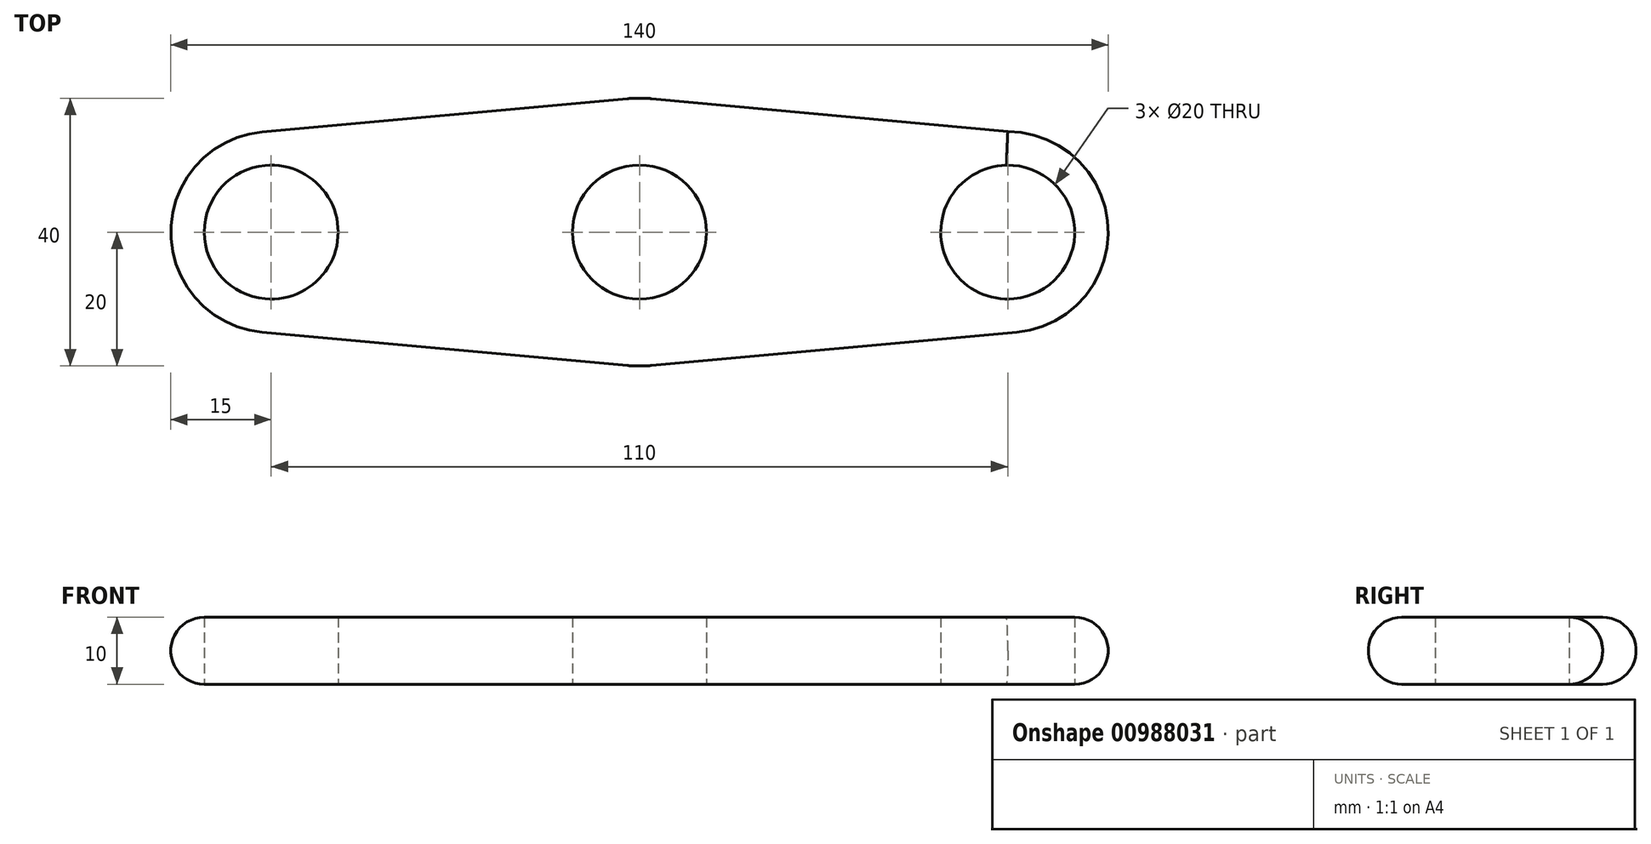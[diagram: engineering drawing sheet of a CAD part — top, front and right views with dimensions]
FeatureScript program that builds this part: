
annotation { "Feature Type Name" : "Feature", "Feature Type Description" : "" }
export const myFeature = defineFeature(function(context is Context, id is Id, definition is map)
    precondition{}
    {
        {
            var Q0;
            Q0=qCreatedBy(makeId("Top.planeOp"),FACE);
            var sketch = newSketch(context, id + "F0", { "sketchPlane" : qUnion([Q0])});
            skCircle(sketch, "E0", {"center": v(0, 0) * mm, "radius": 20 * mm});
            skCircle(sketch, "E1", {"center": v(55, 0) * mm, "radius": 15 * mm});
            skCircle(sketch, "E2", {"center": v(-55, 0) * mm, "radius": 15 * mm});
            skLineSegment(sketch, "E3", {"start": v(1.84, 19.92) * mm, "end": v(55, 15) * mm});
            skLineSegment(sketch, "E4", {"start": v(1.82, -19.92) * mm, "end": v(56.36, -14.94) * mm});
            skLineSegment(sketch, "E5", {"start": v(-1.82, 19.92) * mm, "end": v(-56.36, 14.94) * mm});
            skLineSegment(sketch, "E6", {"start": v(-1.82, -19.92) * mm, "end": v(-56.36, -14.94) * mm});
            skCircle(sketch, "E7", {"center": v(-55, 0) * mm, "radius": 10 * mm});
            skCircle(sketch, "E8", {"center": v(55, 0) * mm, "radius": 10 * mm});
            skCircle(sketch, "E9", {"center": v(0, 0) * mm, "radius": 10 * mm});
            skSolve(sketch);
        }
        {
            var Q0;
            {var subQ0=sQuery(id+"F0.wireOp",EDGE,"E3");Q0=makeQuery(id+"F0.imprint","IMPRINT",FACE,{"disambiguationData":[TD([[makeQuery(id+"F0.imprint","IMPRINT",EDGE,{"derivedFrom":subQ0}),-1.0]])]});}
            var Q1;
            Q1=makeQuery(id+"F0.imprint","IMPRINT",FACE,{"disambiguationData":[TD([[makeQuery(id+"F0.imprint","IMPRINT",EDGE,{"derivedFrom":sQuery(id+"F0.wireOp",EDGE,"E9")}),-1.0]])]});
            var Q2;
            {var subQ0=sQuery(id+"F0.wireOp",EDGE,"E5");Q2=makeQuery(id+"F0.imprint","IMPRINT",FACE,{"disambiguationData":[TD([[makeQuery(id+"F0.imprint","IMPRINT",EDGE,{"derivedFrom":subQ0}),1.0]])]});}
            var Q3;
            Q3=makeQuery(id+"F0.imprint","IMPRINT",FACE,{"disambiguationData":[TD([[makeQuery(id+"F0.imprint","IMPRINT",EDGE,{"derivedFrom":sQuery(id+"F0.wireOp",EDGE,"E7")}),-1.0]])]});
            var Q4;
            Q4=makeQuery(id+"F0.imprint","IMPRINT",FACE,{"disambiguationData":[TD([[makeQuery(id+"F0.imprint","IMPRINT",EDGE,{"derivedFrom":sQuery(id+"F0.wireOp",EDGE,"E8")}),-1.0]])]});
            extrude(context, id + "F1", {"entities" : qUnion([Q0, Q1, Q2, Q3, Q4]), "depth" : 10 * mm, "offsetDistance" : 25 * mm});
        }
        {
            var Q0;
            Q0=makeQuery(id+"F1.opExtrude","CAP_EDGE",EDGE,{"disambiguationData":[OSD([sQuery(id+"F0.wireOp",EDGE,"E6")])],"isStart":true});
            var Q1;
            Q1=makeQuery(id+"F1.opExtrude","CAP_EDGE",EDGE,{"disambiguationData":[OSD([sQuery(id+"F0.wireOp",EDGE,"E4")])],"isStart":false});
            fillet(context, id + "F2", {"entities" : qUnion([Q0, Q1]), "radius" : 5 * mm, "tangentPropagation" : true, "allowEdgeOverflow" : false});
        }
    });
